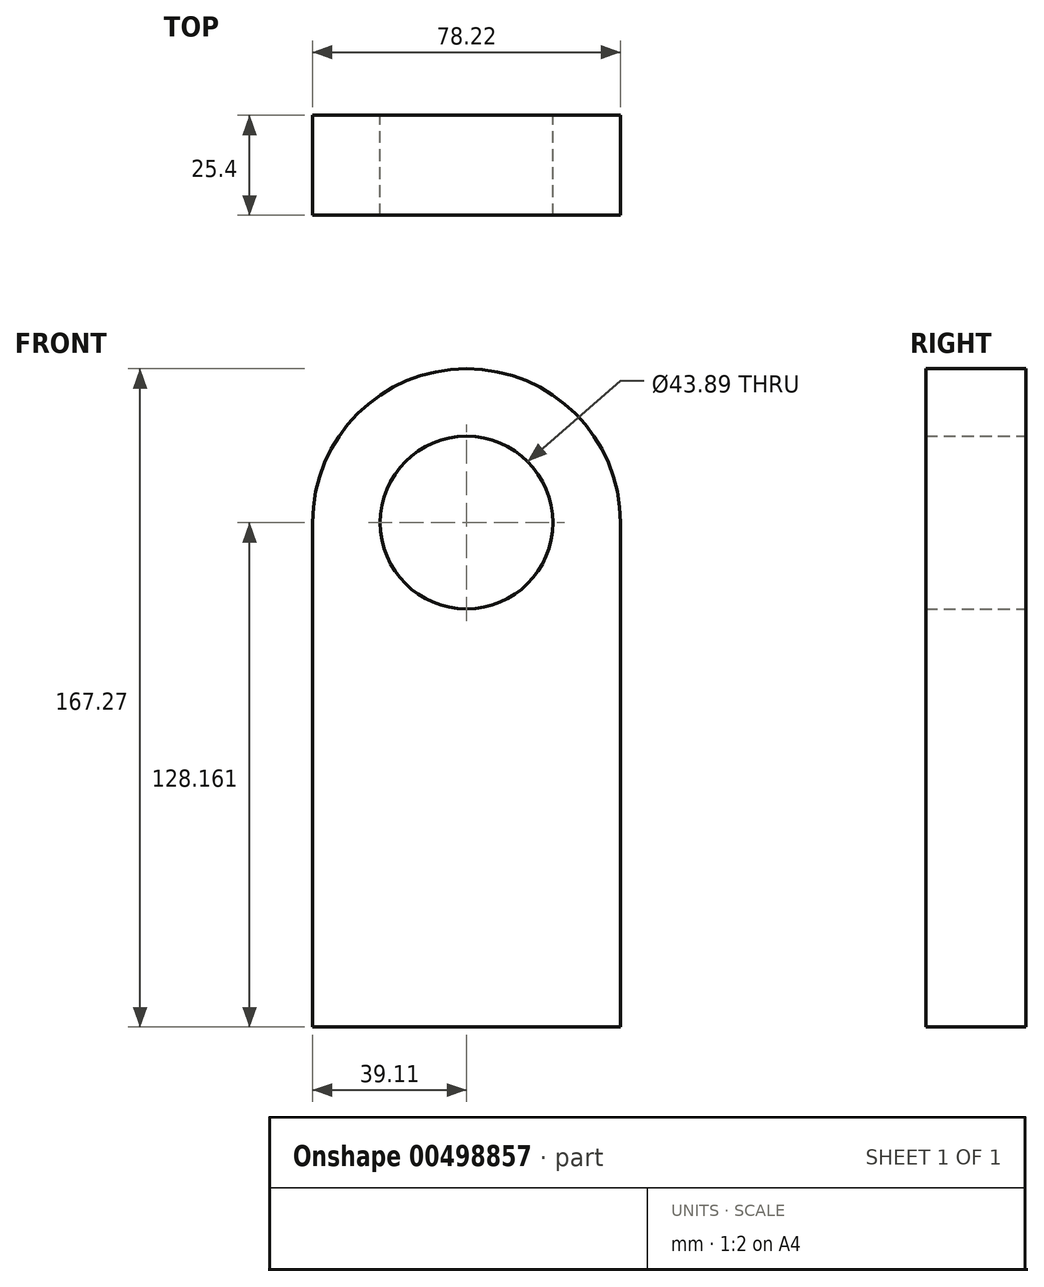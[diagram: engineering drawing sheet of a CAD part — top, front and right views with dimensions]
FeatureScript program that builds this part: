
annotation { "Feature Type Name" : "Feature", "Feature Type Description" : "" }
export const myFeature = defineFeature(function(context is Context, id is Id, definition is map)
    precondition{}
    {
        {
            var Q0;
            Q0=qCreatedBy(makeId("Front.planeOp"),FACE);
            var sketch = newSketch(context, id + "F0", { "sketchPlane" : qUnion([Q0])});
            skLineSegment(sketch, "E0.bottom", {"start": v(39.1, -64.08) * mm, "end": v(-39.1, -64.08) * mm});
            skLineSegment(sketch, "E0.left", {"start": v(39.1, -64.08) * mm, "end": v(39.1, 64.08) * mm});
            skLineSegment(sketch, "E0.right", {"start": v(-39.1, -64.08) * mm, "end": v(-39.1, 64.08) * mm});
            skPoint(sketch, "E0.middle", {"position": v(0, 0) * mm});
            skLineSegment(sketch, "E1", {"start": v(0, 0) * mm, "end": v(0, 42.14) * mm, "construction": true});
            skLineSegment(sketch, "E2", {"start": v(0, 42.14) * mm, "end": v(0, -64.08) * mm, "construction": true});
            skLineSegment(sketch, "E3", {"start": v(-39.1, 0) * mm, "end": v(39.1, 0) * mm, "construction": true});
            skArc(sketch, "E4", {"start": v(39.1, 64.08) * mm, "mid": v(0, 103.19) * mm, "end": v(-39.1, 64.08) * mm});
            skCircle(sketch, "E5", {"center": v(0, 64.08) * mm, "radius": 21.95 * mm});
            skSolve(sketch);
        }
        {
            var Q0;
            Q0=makeQuery(id+"F0.imprint","IMPRINT",FACE,{"disambiguationData":[TD([[makeQuery(id+"F0.imprint","IMPRINT",EDGE,{"derivedFrom":sQuery(id+"F0.wireOp",EDGE,"E0.bottom")}),-1.0]])]});
            extrude(context, id + "F1", {"entities" : qUnion([Q0]), "depth" : 25.4 * mm, "offsetDistance" : 25.4 * mm});
        }
    });
